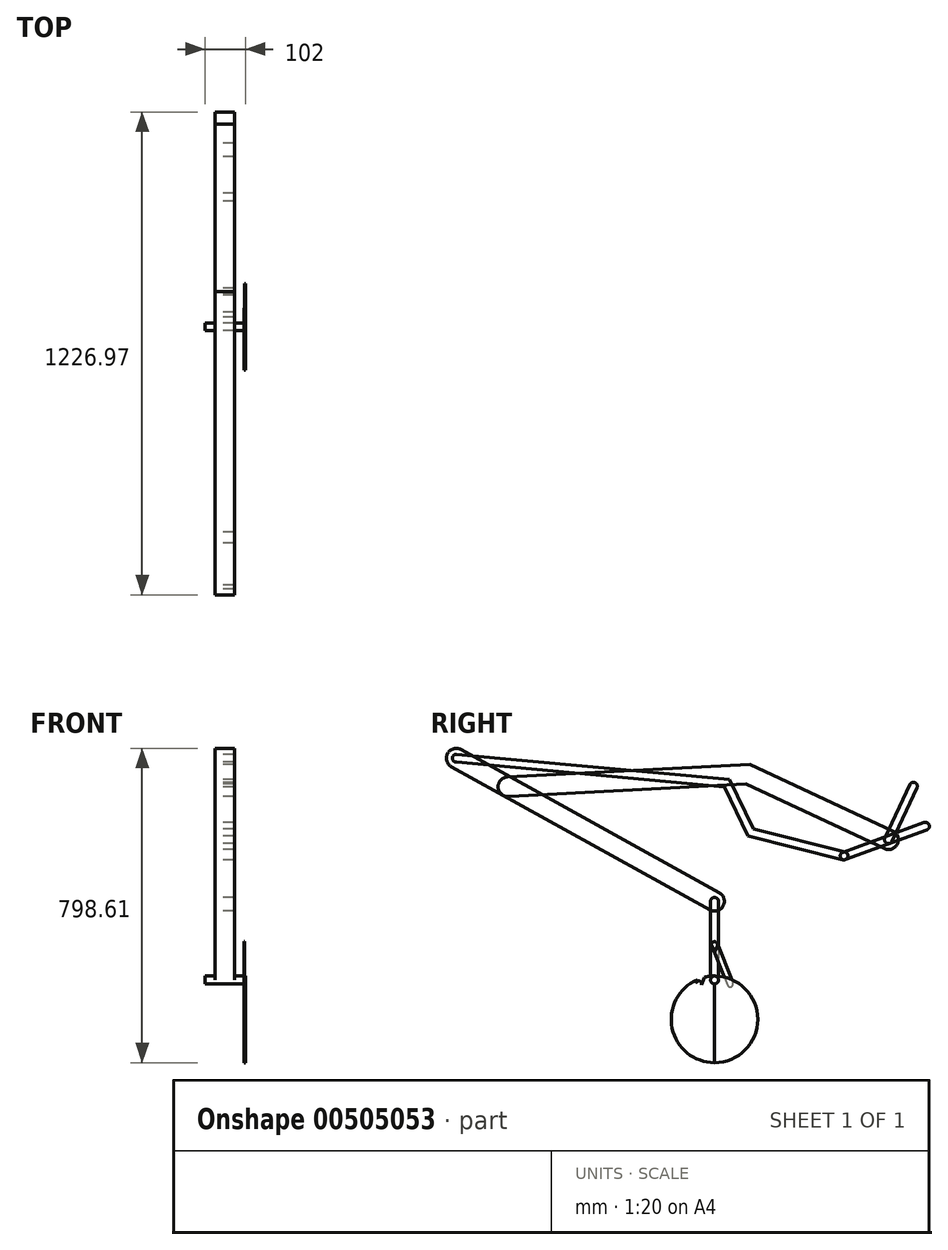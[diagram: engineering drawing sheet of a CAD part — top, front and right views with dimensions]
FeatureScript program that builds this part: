
annotation { "Feature Type Name" : "Feature", "Feature Type Description" : "" }
export const myFeature = defineFeature(function(context is Context, id is Id, definition is map)
    precondition{}
    {
        {
            var Q0;
            Q0=qCreatedBy(makeId("Right.planeOp"),FACE);
            var sketch = newSketch(context, id + "F0", { "sketchPlane" : qUnion([Q0])});
            skCircle(sketch, "E0", {"center": v(0, 0) * mm, "radius": 25 * mm});
            skLineSegment(sketch, "E1", {"start": v(-10.57, -22.66) * mm, "end": v(-361.96, 141.2) * mm});
            skLineSegment(sketch, "E2", {"start": v(10.57, 22.66) * mm, "end": v(-351.96, 191.7) * mm});
            skLineSegment(sketch, "E3", {"start": v(-361.96, 141.2) * mm, "end": v(-963.4, 109.68) * mm});
            skLineSegment(sketch, "E4", {"start": v(-351.96, 191.7) * mm, "end": v(-968.11, 159.41) * mm});
            skPoint(sketch, "E5", {"position": v(-351.96, 191.7) * mm});
            skLineSegment(sketch, "E6", {"start": v(-361.96, 141.2) * mm, "end": v(-351.96, 191.7) * mm});
            skArc(sketch, "E7", {"start": v(-968.11, 159.41) * mm, "mid": v(-991.7, 132.09) * mm, "end": v(-963.4, 109.68) * mm});
            skLineSegment(sketch, "E8", {"start": v(0, 0) * mm, "end": v(0, 0) * mm});
            skLineSegment(sketch, "E9", {"start": v(0, 0) * mm, "end": v(-57.47, 0) * mm, "construction": true});
            skSolve(sketch);
        }
        {
            var Q0;
            Q0=qCreatedBy(makeId("Right.planeOp"),FACE);
            var sketch = newSketch(context, id + "F1", { "sketchPlane" : qUnion([Q0])});
            skPoint(sketch, "E10.0", {"position": v(-966.8, 134.45) * mm});
            skPoint(sketch, "E11.0", {"position": v(-968.11, 159.41) * mm});
            skCircle(sketch, "E12", {"center": v(-442.03, -156.44) * mm, "radius": 25 * mm});
            skLineSegment(sketch, "E13", {"start": v(-429.91, -134.57) * mm, "end": v(-954.68, 156.31) * mm});
            skLineSegment(sketch, "E14", {"start": v(-454.15, -178.3) * mm, "end": v(-978.92, 112.58) * mm});
            skLineSegment(sketch, "E15", {"start": v(-954.68, 156.31) * mm, "end": v(-1085.88, 229.03) * mm});
            skLineSegment(sketch, "E16", {"start": v(-978.92, 112.58) * mm, "end": v(-1110.12, 185.3) * mm});
            skArc(sketch, "E17", {"start": v(-1085.88, 229.03) * mm, "mid": v(-1119.86, 219.29) * mm, "end": v(-1110.12, 185.3) * mm});
            skCircle(sketch, "E18", {"center": v(-966.8, 134.45) * mm, "radius": 25 * mm});
            skLineSegment(sketch, "E19.0", {"start": v(-361.96, 141.2) * mm, "end": v(-963.4, 109.68) * mm, "construction": true});
            skSolve(sketch);
        }
        {
            var Q0;
            Q0=qCreatedBy(makeId("Right.planeOp"),FACE);
            var sketch = newSketch(context, id + "F2", { "sketchPlane" : qUnion([Q0])});
            skCircle(sketch, "E20", {"center": v(0, 0) * mm, "radius": 10 * mm});
            skLineSegment(sketch, "E21", {"start": v(-3.42, 9.4) * mm, "end": v(90.55, 43.6) * mm});
            skLineSegment(sketch, "E22", {"start": v(3.42, -9.4) * mm, "end": v(97.39, 24.8) * mm});
            skArc(sketch, "E23", {"start": v(90.55, 43.6) * mm, "mid": v(103.37, 37.62) * mm, "end": v(97.39, 24.8) * mm});
            skLineSegment(sketch, "E24", {"start": v(-3.42, 9.4) * mm, "end": v(-116.18, -31.65) * mm});
            skLineSegment(sketch, "E25", {"start": v(3.42, -9.4) * mm, "end": v(-109.34, -50.44) * mm});
            skArc(sketch, "E26", {"start": v(-116.18, -31.65) * mm, "mid": v(-122.16, -44.46) * mm, "end": v(-109.34, -50.44) * mm});
            skLineSegment(sketch, "E27", {"start": v(0, 0) * mm, "end": v(97.6, 0) * mm, "construction": true});
            skSolve(sketch);
        }
        {
            var Q0;
            Q0=qCreatedBy(makeId("Right.planeOp"),FACE);
            var sketch = newSketch(context, id + "F3", { "sketchPlane" : qUnion([Q0])});
            skPoint(sketch, "E28.0", {"position": v(-112.76, -41.04) * mm});
            skCircle(sketch, "E29", {"center": v(-112.76, -41.04) * mm, "radius": 10 * mm});
            skPoint(sketch, "E30.0", {"position": v(-1098, 207.17) * mm});
            skCircle(sketch, "E31", {"center": v(-1098, 207.17) * mm, "radius": 10 * mm});
            skLineSegment(sketch, "E32", {"start": v(-115.2, -50.74) * mm, "end": v(-356.98, 10.17) * mm});
            skLineSegment(sketch, "E33", {"start": v(-343.05, 27.29) * mm, "end": v(-404.11, 153.27) * mm});
            skLineSegment(sketch, "E34", {"start": v(-404.11, 153.27) * mm, "end": v(-1097.08, 217.13) * mm});
            skLineSegment(sketch, "E35", {"start": v(-1100.44, 197.47) * mm, "end": v(-417.25, 134.51) * mm});
            skLineSegment(sketch, "E36", {"start": v(-417.25, 134.51) * mm, "end": v(-356.98, 10.17) * mm});
            skLineSegment(sketch, "E37", {"start": v(-381.43, 106.47) * mm, "end": v(-399.43, 97.75) * mm, "construction": true});
            skLineSegment(sketch, "E38.trimOffspring", {"start": v(-343.05, 27.29) * mm, "end": v(-110.32, -31.35) * mm});
            skSolve(sketch);
        }
        {
            var Q0;
            Q0 = qSketchRegion(id + "F0", true);
            extrude(context, id + "F4", {"entities" : qUnion([Q0]), "endBound" : BoundingType.SYMMETRIC, "depth" : 50 * mm});
        }
        {
            var Q0;
            Q0 = qSketchRegion(id + "F1", true);
            extrude(context, id + "F5", {"entities" : qUnion([Q0]), "endBound" : BoundingType.SYMMETRIC, "depth" : 50 * mm});
        }
        {
            var Q0;
            Q0 = qSketchRegion(id + "F2", true);
            extrude(context, id + "F6", {"entities" : qUnion([Q0]), "endBound" : BoundingType.SYMMETRIC, "depth" : 50 * mm});
        }
        {
            var Q0;
            Q0 = qSketchRegion(id + "F3", true);
            extrude(context, id + "F7", {"entities" : qUnion([Q0]), "endBound" : BoundingType.SYMMETRIC, "depth" : 50 * mm});
        }
        {
            var Q0;
            Q0=qCreatedBy(makeId("Right.planeOp"),FACE);
            var sketch = newSketch(context, id + "F8", { "sketchPlane" : qUnion([Q0])});
            skPoint(sketch, "E39.0", {"position": v(0, 0) * mm});
            skCircle(sketch, "E40", {"center": v(0, 0) * mm, "radius": 10 * mm});
            skLineSegment(sketch, "E41.0", {"start": v(10.57, 22.66) * mm, "end": v(-351.96, 191.7) * mm, "construction": true});
            skLineSegment(sketch, "E42", {"start": v(-9.06, 4.23) * mm, "end": v(54.33, 140.17) * mm});
            skLineSegment(sketch, "E43", {"start": v(9.06, -4.23) * mm, "end": v(72.46, 131.72) * mm});
            skArc(sketch, "E44", {"start": v(54.33, 140.17) * mm, "mid": v(67.62, 145) * mm, "end": v(72.46, 131.72) * mm});
            skSolve(sketch);
        }
        {
            var Q0;
            Q0 = qSketchRegion(id + "F8", true);
            extrude(context, id + "F9", {"entities" : qUnion([Q0]), "endBound" : BoundingType.SYMMETRIC, "depth" : 50 * mm});
        }
        {
            var Q0;
            Q0=qCreatedBy(makeId("Right.planeOp"),FACE);
            var sketch = newSketch(context, id + "F10", { "sketchPlane" : qUnion([Q0])});
            skPoint(sketch, "E45.0", {"position": v(-442.03, -156.44) * mm});
            skCircle(sketch, "E46", {"center": v(-442.03, -156.44) * mm, "radius": 10 * mm});
            skLineSegment(sketch, "E47", {"start": v(-452.03, -156.44) * mm, "end": v(-452.03, -356.44) * mm});
            skLineSegment(sketch, "E48", {"start": v(-432.03, -156.44) * mm, "end": v(-432.03, -356.44) * mm});
            skArc(sketch, "E49", {"start": v(-452.03, -356.44) * mm, "mid": v(-442.03, -366.44) * mm, "end": v(-432.03, -356.44) * mm});
            skCircle(sketch, "E50", {"center": v(-442.03, -356.44) * mm, "radius": 10 * mm});
            skSolve(sketch);
        }
        {
            var Q0;
            {var subQ0=sQuery(id+"F10.wireOp",EDGE,"E47");Q0=makeQuery(id+"F10.imprint","IMPRINT",FACE,{"disambiguationData":[TD([[makeQuery(id+"F10.imprint","IMPRINT",EDGE,{"derivedFrom":subQ0}),1.0]])]});}
            var Q1;
            {var subQ0=sQuery(id+"F10.wireOp",EDGE,"E50");var subQ1=makeQuery(id+"F10.imprint","INTERSECT",VERTEX,{"derivedFrom":[sQuery(id+"F10.wireOp",EDGE,"E47"),subQ0]});Q1=makeQuery(id+"F10.imprint","IMPRINT",FACE,{"disambiguationData":[TD([[makeQuery(id+"F10.imprint","IMPRINT",EDGE,{"disambiguationData":[TD([[subQ1,1.0]])],"derivedFrom":subQ0}),1.0]])]});}
            var Q2;
            {var subQ0=sQuery(id+"F10.wireOp",EDGE,"E46");var subQ1=makeQuery(id+"F10.imprint","INTERSECT",VERTEX,{"derivedFrom":[subQ0,sQuery(id+"F10.wireOp",EDGE,"E47")]});Q2=makeQuery(id+"F10.imprint","IMPRINT",FACE,{"disambiguationData":[TD([[makeQuery(id+"F10.imprint","IMPRINT",EDGE,{"disambiguationData":[TD([[subQ1,1.0]])],"derivedFrom":subQ0}),1.0]])]});}
            extrude(context, id + "F11", {"entities" : qUnion([Q0, Q1, Q2]), "endBound" : BoundingType.SYMMETRIC, "depth" : 50 * mm});
        }
        {
            var Q0;
            {var subQ0=sQuery(id+"F10.wireOp",EDGE,"E50");var subQ1=makeQuery(id+"F10.imprint","INTERSECT",VERTEX,{"derivedFrom":[sQuery(id+"F10.wireOp",EDGE,"E47"),subQ0]});Q0=makeQuery(id+"F10.imprint","IMPRINT",FACE,{"disambiguationData":[TD([[makeQuery(id+"F10.imprint","IMPRINT",EDGE,{"disambiguationData":[TD([[subQ1,1.0]])],"derivedFrom":subQ0}),1.0]])]});}
            extrude(context, id + "F12", {"entities" : qUnion([Q0]), "operationType" : NewBodyOperationType.ADD, "endBound" : BoundingType.SYMMETRIC, "depth" : 100 * mm});
        }
        {
            var Q0;
            Q0=makeQuery(id+"F12.opExtrude","CAP_FACE",FACE,{"disambiguationData":[OSD([sQuery(id+"F10.wireOp",EDGE,"E50")])],"isStart":false});
            var sketch = newSketch(context, id + "F13", { "sketchPlane" : qUnion([Q0])});
            skPoint(sketch, "E51.0", {"position": v(-442.03, -356.44) * mm});
            skCircle(sketch, "E52.0", {"center": v(-442.03, -356.44) * mm, "radius": 10 * mm});
            skLineSegment(sketch, "E53", {"start": v(-442.03, -366.44) * mm, "end": v(-442.03, -566.44) * mm});
            skArc(sketch, "E54", {"start": v(-442.03, -566.44) * mm, "mid": v(-332.03, -456.44) * mm, "end": v(-442.03, -346.44) * mm});
            skArc(sketch, "E55.MirrorCS", {"start": v(-442.03, -566.44) * mm, "mid": v(-552.03, -456.44) * mm, "end": v(-442.03, -346.44) * mm});
            skLineSegment(sketch, "E56", {"start": v(-442.03, -366.44) * mm, "end": v(-482.03, -366.44) * mm, "construction": true});
            skLineSegment(sketch, "E57", {"start": v(-442.03, -366.44) * mm, "end": v(-402.03, -366.44) * mm, "construction": true});
            skCircle(sketch, "E58", {"center": v(-482.03, -366.44) * mm, "radius": 7.5 * mm});
            skCircle(sketch, "E59", {"center": v(-402.03, -366.44) * mm, "radius": 7.5 * mm});
            skLineSegment(sketch, "E60", {"start": v(-442.03, -366.44) * mm, "end": v(-442.03, -266.44) * mm, "construction": true});
            skCircle(sketch, "E61", {"center": v(-442.03, -266.44) * mm, "radius": 7.5 * mm});
            skLineSegment(sketch, "E62", {"start": v(-449, -263.65) * mm, "end": v(-489, -363.65) * mm});
            skLineSegment(sketch, "E63", {"start": v(-475.07, -369.22) * mm, "end": v(-435.07, -269.22) * mm});
            skLineSegment(sketch, "E64", {"start": v(-449, -269.22) * mm, "end": v(-409, -369.22) * mm});
            skLineSegment(sketch, "E65", {"start": v(-435.07, -263.65) * mm, "end": v(-395.07, -363.65) * mm});
            skSolve(sketch);
        }
        {
            var Q0;
            {var subQ0=sQuery(id+"F13.wireOp",EDGE,"E53");Q0=makeQuery(id+"F13.imprint","IMPRINT",FACE,{"disambiguationData":[TD([[makeQuery(id+"F13.imprint","IMPRINT",EDGE,{"derivedFrom":subQ0}),-1.0]])]});}
            var Q1;
            {var subQ0=sQuery(id+"F13.wireOp",EDGE,"E52.0");var subQ1=makeQuery(id+"F13.imprint","INTERSECT",VERTEX,{"derivedFrom":[subQ0,sQuery(id+"F13.wireOp",EDGE,"E53")]});Q1=makeQuery(id+"F13.imprint","IMPRINT",FACE,{"disambiguationData":[TD([[makeQuery(id+"F13.imprint","IMPRINT",EDGE,{"disambiguationData":[TD([[subQ1,1.0]])],"derivedFrom":subQ0}),1.0]])]});}
            var Q2;
            {var subQ0=sQuery(id+"F13.wireOp",EDGE,"E58");var subQ1=makeQuery(id+"F13.imprint","INTERSECT",VERTEX,{"derivedFrom":[subQ0,sQuery(id+"F13.wireOp",EDGE,"E62")]});Q2=makeQuery(id+"F13.imprint","IMPRINT",FACE,{"disambiguationData":[TD([[makeQuery(id+"F13.imprint","IMPRINT",EDGE,{"disambiguationData":[TD([[subQ1,-1.0]])],"derivedFrom":subQ0}),1.0]])]});}
            var Q3;
            {var subQ0=sQuery(id+"F13.wireOp",EDGE,"E62");var subQ1=sQuery(id+"F13.wireOp",EDGE,"E55.MirrorCS");var subQ2=makeQuery(id+"F13.imprint","INTERSECT",VERTEX,{"derivedFrom":[subQ1,subQ0]});Q3=makeQuery(id+"F13.imprint","IMPRINT",FACE,{"disambiguationData":[TD([[makeQuery(id+"F13.imprint","IMPRINT",EDGE,{"disambiguationData":[TD([[subQ2,-1.0]])],"derivedFrom":subQ1}),-1.0]])]});}
            extrude(context, id + "F14", {"entities" : qUnion([Q0, Q1, Q2, Q3]), "depth" : 2 * mm});
        }
        {
            var Q0;
            {var subQ0=sQuery(id+"F13.wireOp",EDGE,"E53");Q0=makeQuery(id+"F13.imprint","IMPRINT",FACE,{"disambiguationData":[TD([[makeQuery(id+"F13.imprint","IMPRINT",EDGE,{"derivedFrom":subQ0}),1.0]])]});}
            var Q1;
            {var subQ0=sQuery(id+"F13.wireOp",EDGE,"E52.0");var subQ1=makeQuery(id+"F13.imprint","INTERSECT",VERTEX,{"derivedFrom":[subQ0,sQuery(id+"F13.wireOp",EDGE,"E53")]});Q1=makeQuery(id+"F13.imprint","IMPRINT",FACE,{"disambiguationData":[TD([[makeQuery(id+"F13.imprint","IMPRINT",EDGE,{"disambiguationData":[TD([[subQ1,1.0]])],"derivedFrom":subQ0}),1.0]])]});}
            var Q2;
            {var subQ0=sQuery(id+"F13.wireOp",EDGE,"E59");var subQ1=makeQuery(id+"F13.imprint","INTERSECT",VERTEX,{"derivedFrom":[subQ0,sQuery(id+"F13.wireOp",EDGE,"E64")]});Q2=makeQuery(id+"F13.imprint","IMPRINT",FACE,{"disambiguationData":[TD([[makeQuery(id+"F13.imprint","IMPRINT",EDGE,{"disambiguationData":[TD([[subQ1,1.0]])],"derivedFrom":subQ0}),1.0]])]});}
            var Q3;
            {var subQ0=sQuery(id+"F13.wireOp",EDGE,"E65");var subQ1=sQuery(id+"F13.wireOp",EDGE,"E54");var subQ2=makeQuery(id+"F13.imprint","INTERSECT",VERTEX,{"derivedFrom":[subQ1,subQ0]});Q3=makeQuery(id+"F13.imprint","IMPRINT",FACE,{"disambiguationData":[TD([[makeQuery(id+"F13.imprint","IMPRINT",EDGE,{"disambiguationData":[TD([[subQ2,-1.0]])],"derivedFrom":subQ1}),1.0]])]});}
            extrude(context, id + "F15", {"entities" : qUnion([Q0, Q1, Q2, Q3]), "depth" : 2 * mm});
        }
        {
            var Q0;
            {var subQ0=sQuery(id+"F13.wireOp",EDGE,"E58");var subQ1=makeQuery(id+"F13.imprint","INTERSECT",VERTEX,{"derivedFrom":[subQ0,sQuery(id+"F13.wireOp",EDGE,"E62")]});Q0=makeQuery(id+"F13.imprint","IMPRINT",FACE,{"disambiguationData":[TD([[makeQuery(id+"F13.imprint","IMPRINT",EDGE,{"disambiguationData":[TD([[subQ1,-1.0]])],"derivedFrom":subQ0}),1.0]])]});}
            var Q1;
            {var subQ0=sQuery(id+"F13.wireOp",EDGE,"E62");var subQ1=sQuery(id+"F13.wireOp",EDGE,"E55.MirrorCS");var subQ2=makeQuery(id+"F13.imprint","INTERSECT",VERTEX,{"derivedFrom":[subQ1,subQ0]});Q1=makeQuery(id+"F13.imprint","IMPRINT",FACE,{"disambiguationData":[TD([[makeQuery(id+"F13.imprint","IMPRINT",EDGE,{"disambiguationData":[TD([[subQ2,-1.0]])],"derivedFrom":subQ1}),-1.0]])]});}
            var Q2;
            {var subQ1=sQuery(id+"F13.wireOp",EDGE,"E55.MirrorCS");var subQ5=sQuery(id+"F13.wireOp",EDGE,"E62");var subQ9=makeQuery(id+"F13.imprint","INTERSECT",VERTEX,{"derivedFrom":[subQ1,subQ5]});Q2=makeQuery(id+"F13.imprint","IMPRINT",FACE,{"disambiguationData":[TD([[makeQuery(id+"F13.imprint","IMPRINT",EDGE,{"disambiguationData":[TD([[subQ9,-1.0]])],"derivedFrom":subQ1}),1.0]])]});}
            var Q3;
            {var subQ0=sQuery(id+"F13.wireOp",EDGE,"E61");var subQ1=makeQuery(id+"F13.imprint","INTERSECT",VERTEX,{"derivedFrom":[subQ0,sQuery(id+"F13.wireOp",EDGE,"E62")]});Q3=makeQuery(id+"F13.imprint","IMPRINT",FACE,{"disambiguationData":[TD([[makeQuery(id+"F13.imprint","IMPRINT",EDGE,{"disambiguationData":[TD([[subQ1,1.0]])],"derivedFrom":subQ0}),1.0]])]});}
            var Q4;
            {var subQ0=sQuery(id+"F13.wireOp",EDGE,"E63");var subQ1=sQuery(id+"F13.wireOp",EDGE,"E61");var subQ2=makeQuery(id+"F13.imprint","INTERSECT",VERTEX,{"derivedFrom":[subQ1,subQ0]});Q4=makeQuery(id+"F13.imprint","IMPRINT",FACE,{"disambiguationData":[TD([[makeQuery(id+"F13.imprint","IMPRINT",EDGE,{"disambiguationData":[TD([[subQ2,1.0]])],"derivedFrom":subQ1}),-1.0]])]});}
            extrude(context, id + "F16", {"entities" : qUnion([Q0, Q1, Q2, Q3, Q4]), "oppositeDirection" : true, "depth" : 2 * mm});
        }
        {
            var Q0;
            {var subQ0=sQuery(id+"F13.wireOp",EDGE,"E59");var subQ1=makeQuery(id+"F13.imprint","INTERSECT",VERTEX,{"derivedFrom":[subQ0,sQuery(id+"F13.wireOp",EDGE,"E64")]});Q0=makeQuery(id+"F13.imprint","IMPRINT",FACE,{"disambiguationData":[TD([[makeQuery(id+"F13.imprint","IMPRINT",EDGE,{"disambiguationData":[TD([[subQ1,1.0]])],"derivedFrom":subQ0}),1.0]])]});}
            var Q1;
            {var subQ1=sQuery(id+"F13.wireOp",EDGE,"E54");var subQ7=sQuery(id+"F13.wireOp",EDGE,"E65");var subQ9=makeQuery(id+"F13.imprint","INTERSECT",VERTEX,{"derivedFrom":[subQ1,subQ7]});Q1=makeQuery(id+"F13.imprint","IMPRINT",FACE,{"disambiguationData":[TD([[makeQuery(id+"F13.imprint","IMPRINT",EDGE,{"disambiguationData":[TD([[subQ9,-1.0]])],"derivedFrom":subQ1}),-1.0]])]});}
            var Q2;
            {var subQ0=sQuery(id+"F13.wireOp",EDGE,"E65");var subQ1=sQuery(id+"F13.wireOp",EDGE,"E54");var subQ2=makeQuery(id+"F13.imprint","INTERSECT",VERTEX,{"derivedFrom":[subQ1,subQ0]});Q2=makeQuery(id+"F13.imprint","IMPRINT",FACE,{"disambiguationData":[TD([[makeQuery(id+"F13.imprint","IMPRINT",EDGE,{"disambiguationData":[TD([[subQ2,-1.0]])],"derivedFrom":subQ1}),1.0]])]});}
            var Q3;
            {var subQ0=sQuery(id+"F13.wireOp",EDGE,"E63");var subQ1=sQuery(id+"F13.wireOp",EDGE,"E61");var subQ2=makeQuery(id+"F13.imprint","INTERSECT",VERTEX,{"derivedFrom":[subQ1,subQ0]});Q3=makeQuery(id+"F13.imprint","IMPRINT",FACE,{"disambiguationData":[TD([[makeQuery(id+"F13.imprint","IMPRINT",EDGE,{"disambiguationData":[TD([[subQ2,1.0]])],"derivedFrom":subQ1}),-1.0]])]});}
            var Q4;
            {var subQ0=sQuery(id+"F13.wireOp",EDGE,"E61");var subQ1=makeQuery(id+"F13.imprint","INTERSECT",VERTEX,{"derivedFrom":[subQ0,sQuery(id+"F13.wireOp",EDGE,"E62")]});Q4=makeQuery(id+"F13.imprint","IMPRINT",FACE,{"disambiguationData":[TD([[makeQuery(id+"F13.imprint","IMPRINT",EDGE,{"disambiguationData":[TD([[subQ1,1.0]])],"derivedFrom":subQ0}),1.0]])]});}
            extrude(context, id + "F17", {"entities" : qUnion([Q0, Q1, Q2, Q3, Q4]), "oppositeDirection" : true, "depth" : 2 * mm});
        }
    });
